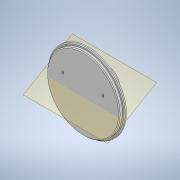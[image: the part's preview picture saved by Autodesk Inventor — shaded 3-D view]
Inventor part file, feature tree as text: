
AUTODESK INVENTOR PART (.ipt)
format: ipt  version: 2021 (Build 250183000, 183)  size: 169,472 bytes
history: native  units: in
note: dims shown in document units (in); Inventor stores cm internally (conversion verified against a paired STEP export)
features: extrude x4, sketch x4, chamfer x2, fillet x1, plane x1, mirror x1, projected_geometry x1
ambient origin geometry x8: Origin, YZ Plane, XZ Plane, XY Plane, X Axis, Y Axis, Z Axis, Center Point
bodies: Solid1 (feature_tree)
feature tree (14):
  extrude  "Extrusion1"  Depth=0.0394in TaperAngle=0.0deg
  extrude  "Extrusion2"  Depth=0.0591in TaperAngle=0.0deg
  chamfer  "Chamfer1"  Distance=0.0787in Angle=45.0deg
  chamfer  "Chamfer2"  Distance=0.0787in Angle=45.0deg
  extrude  "Extrusion3"  Depth=0.3937in
  fillet  "Fillet1"  Radius=0.1969in
  plane  "Work Plane1"
  extrude  "Extrusion4"  Depth=0.3937in
  mirror  "Mirror1"
  sketch  "Sketch1"  dims[d0=1.4961in d1=0.0394in d2=0.0in]
  sketch  "Sketch2"  dims[d3=1.4134in d4=0.0591in d5=0.0in d6=0.0157in d7=0.0787in d8=45.0deg d9=0.0157in d10=0.0787in d11=45.0deg]
  sketch  "Sketch3"  dims[d12=0.1575in d13=0.3937in d14=0.1374in d15=0.1969in]
  sketch  "Sketch4"  dims[d16=30.0deg d17=0.0295in d18=0.3937in d19=0.0in d20=0.0in]
  projected_geometry  "Projected Loop1"
